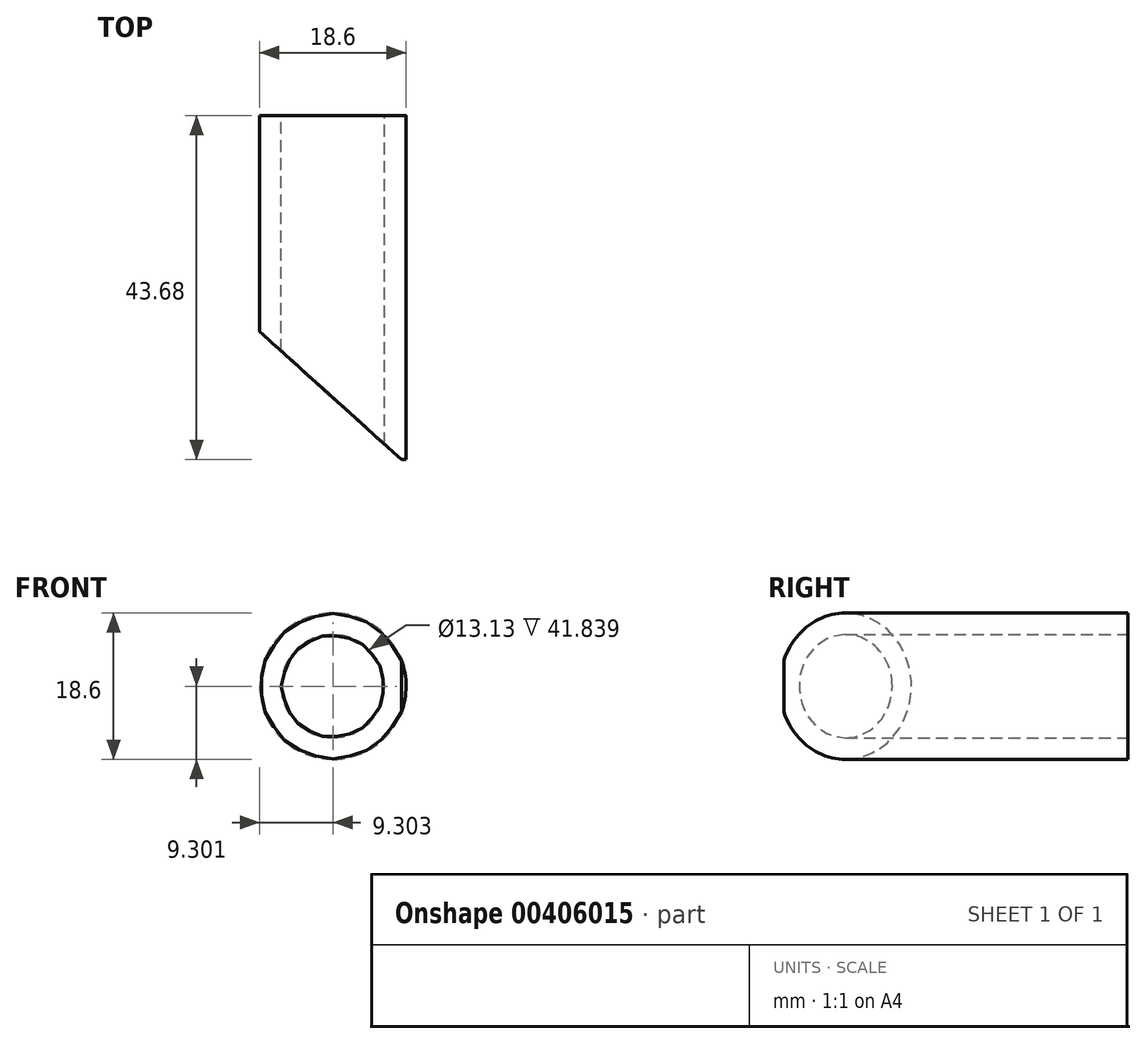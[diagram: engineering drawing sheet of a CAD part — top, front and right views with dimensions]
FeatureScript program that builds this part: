
annotation { "Feature Type Name" : "Feature", "Feature Type Description" : "" }
export const myFeature = defineFeature(function(context is Context, id is Id, definition is map)
    precondition{}
    {
        {
            var Q0;
            Q0=qCreatedBy(makeId("Front.planeOp"),FACE);
            var sketch = newSketch(context, id + "F0", { "sketchPlane" : qUnion([Q0])});
            skCircle(sketch, "E0", {"center": v(-16.84, 12.95) * mm, "radius": 9.3 * mm});
            skCircle(sketch, "E1", {"center": v(-16.84, 12.95) * mm, "radius": 6.56 * mm});
            skSolve(sketch);
        }
        {
            var Q0;
            Q0 = qSketchRegion(id + "F0", true);
            extrude(context, id + "F1", {"entities" : qUnion([Q0]), "endBound" : BoundingType.SYMMETRIC, "depth" : 43.69 * mm});
        }
        {
            var Q0;
            Q0=qCreatedBy(makeId("Top.planeOp"),FACE);
            var sketch = newSketch(context, id + "F2", { "sketchPlane" : qUnion([Q0])});
            skLineSegment(sketch, "E2", {"start": v(0, -29.19) * mm, "end": v(-33.08, -29.19) * mm});
            skLineSegment(sketch, "E3", {"start": v(-33.08, -29.19) * mm, "end": v(-33.08, 0.67) * mm});
            skLineSegment(sketch, "E4", {"start": v(-33.08, 0.67) * mm, "end": v(0, -29.19) * mm});
            skSolve(sketch);
        }
        {
            var Q0;
            Q0 = qSketchRegion(id + "F2", true);
            extrude(context, id + "F3", {"entities" : qUnion([Q0]), "operationType" : NewBodyOperationType.REMOVE, "depth" : 25.4 * mm});
        }
    });
